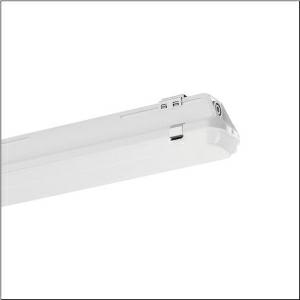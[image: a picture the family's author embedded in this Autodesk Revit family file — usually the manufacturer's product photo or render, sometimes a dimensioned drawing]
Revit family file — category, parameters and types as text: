
# Revit family: monsun_r__21_parking_51fg20dl430k_fea0
name_source: partatom
category: Lighting Fixtures
units: mm (PartAtom-declared; Revit-internal decimal feet)

## family parameters
Cut with Voids When Loaded = No
Host = Face
Light Source = No
Part Type = Normal
Room Calculation Point = No
Round Connector Dimension = Use Diameter
Shared = No

## types (1)
- --- (1 x LED, 3850 lm, 24 W, 4000K)
    Apparent Load = 24 VA
    CIE Flux Codes = 45 75 93 94 100
    Color Rendering = 80
    Color Temperature = 4000K
    Default Elevation = 1800 mm
    Description = Monsun® 21 parking, damp-proof luminaire, chain hanger, primary optical cover: enclosure, of PC, light emission: direct distribution, primary light characteristic: symmetric, installation type: suspended mounting, surface-mounted, horizontal mounting, vertical mounting, LED, rated luminous flux: 3.850lm, luminous efficacy: 160lm/W, light colour: 840, colour temperature: 4000K, control gear: DALI 2, with terminal, 5-pole, max. 2.5mm², mains connection: 220..240V, AC, 50/60Hz, rated input power: 24W, housing, of glass-fibre reinforced plastic, uncoated, bright grey, incl. chain hanger, length: 1.299mm, width: 90mm, height: 88mm, clip for enclosure, of stainless steel (V2A), ceiling mounting element, of stainless steel (V2A), chain hanger, of stainless steel (V2A), protection rating (complete): IP66, insulation class (complete): insulation class I (protective earthing), certification: CE, ENEC, VDE, UKCA, protection symbol: D, impact resistance: IK08, permissible operating ambient temperature: -25..+35°C, standard: EN 50419, EN 60598-2-1, corresponds to IFS (International Featured Standards) requirements for safety and quality in the food industry, for indoor or canopied outdoor use, no direct snow, no direct sun, no direct rain, LABS conformity tested according to VDMA 24364:2018-05, contact your sales advisor before using the luminaires in applications with unclear chemical exposure, large temperature fluctuations or condensation-forming humidity, packaging unit: 1 piece
    Height = 88 mm
    Lamp = 1 x LED
    Lamp Light Flux = 3850 lm
    Lamp Power = 24 W
    Lamp count = 1
    Length = 1299 mm
    Luminous efficacy = 160 lm/W
    Manufacturer = Siteco
    ModVariant = No
    Model = 51FG20DL430K
    Mounting Place = Ceiling
    Mounting Type = Surface mounted
    Number of Poles = 1
    OnlyDefault = Yes
    Power Factor = 1
    Product Name = Monsun® 21 parking
    Product group = damp-proof luminaire
    ProductGroupID = 300
    Protection Class = Protection class I
    Protection Degree = IP 66
    RLX_Detail_Level = 1
    RLX_Emergency_Light_Flux = 0 lm
    RLX_Emergency_Type = 0
    RLX_Emergency_Type_DB = No
    RlxData = <blob elided: 93417 chars, md5=f07f431d>
    Socket = socket
    Standby Power = 0 W
    System Light Flux = 3850 lm
    System Power = 24 W
    Type Comments = factory setting: luminous flux: 100 % | dim-lin: 254 | 161 mA
    Type Image = l_1319656.jpg
    URL = http://relux.com
    VarID = @adj_022406
    Voltage = 0 V
    Weight = 0.00 kg
    Width = 90 mm

## geometry (parser evidence)
native form markers: Blend x4, Sweep x13
no freeform markers — native parametric forms only
